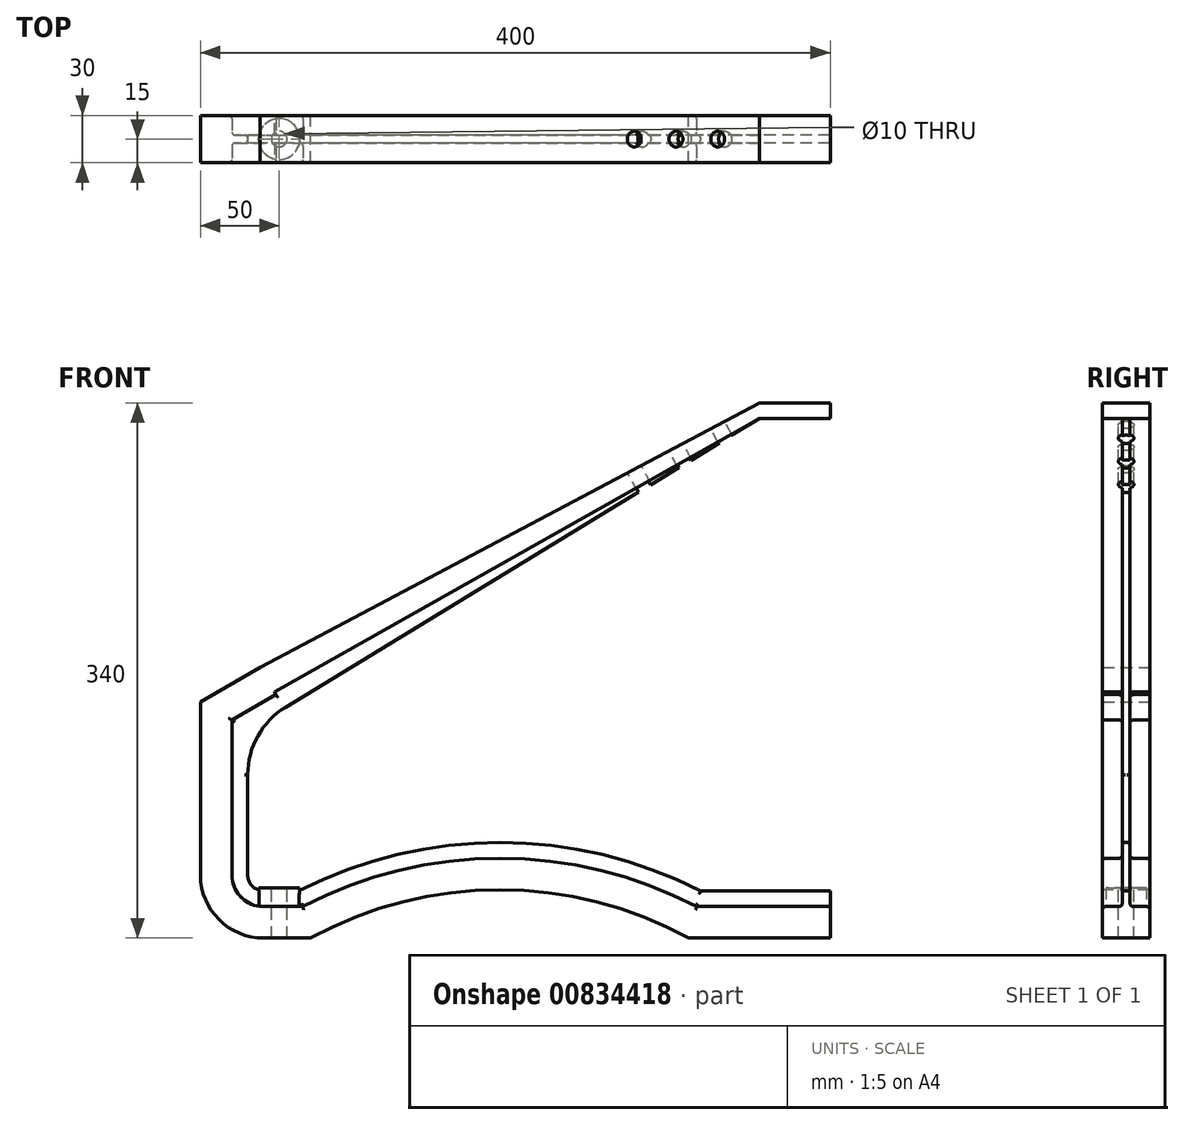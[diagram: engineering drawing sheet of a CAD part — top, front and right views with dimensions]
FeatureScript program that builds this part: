
annotation { "Feature Type Name" : "Feature", "Feature Type Description" : "" }
export const myFeature = defineFeature(function(context is Context, id is Id, definition is map)
    precondition{}
    {
        {
            var Q0;
            Q0=qCreatedBy(makeId("Right.planeOp"),FACE);
            var sketch = newSketch(context, id + "F0", { "sketchPlane" : qUnion([Q0])});
            skLineSegment(sketch, "E0", {"start": v(-15, 0) * mm, "end": v(15, 0) * mm});
            skLineSegment(sketch, "E1", {"start": v(15, 0) * mm, "end": v(15, 18) * mm});
            skLineSegment(sketch, "E2", {"start": v(13, 20) * mm, "end": v(4.5, 20) * mm});
            skLineSegment(sketch, "E3", {"start": v(2.5, 22) * mm, "end": v(2.5, 28) * mm});
            skLineSegment(sketch, "E4", {"start": v(0.5, 30) * mm, "end": v(-0.5, 30) * mm});
            skLineSegment(sketch, "E5", {"start": v(-2.5, 28) * mm, "end": v(-2.5, 22) * mm});
            skLineSegment(sketch, "E6", {"start": v(-4.5, 20) * mm, "end": v(-13, 20) * mm});
            skLineSegment(sketch, "E7", {"start": v(-15, 18) * mm, "end": v(-15, 0) * mm});
            skPoint(sketch, "E8.visualSharp", {"position": v(-15, 20) * mm});
            skArc(sketch, "E8.filletArc", {"start": v(-13, 20) * mm, "mid": v(-14.41, 19.41) * mm, "end": v(-15, 18) * mm});
            skPoint(sketch, "E9.visualSharp", {"position": v(15, 20) * mm});
            skArc(sketch, "E9.filletArc", {"start": v(15, 18) * mm, "mid": v(14.41, 19.41) * mm, "end": v(13, 20) * mm});
            skPoint(sketch, "E10.visualSharp", {"position": v(2.5, 20) * mm});
            skArc(sketch, "E10.filletArc", {"start": v(2.5, 22) * mm, "mid": v(3.09, 20.59) * mm, "end": v(4.5, 20) * mm});
            skPoint(sketch, "E11.visualSharp", {"position": v(-2.5, 20) * mm});
            skArc(sketch, "E11.filletArc", {"start": v(-4.5, 20) * mm, "mid": v(-3.09, 20.59) * mm, "end": v(-2.5, 22) * mm});
            skPoint(sketch, "E12.visualSharp", {"position": v(-2.5, 30) * mm});
            skArc(sketch, "E12.filletArc", {"start": v(-0.5, 30) * mm, "mid": v(-1.91, 29.41) * mm, "end": v(-2.5, 28) * mm});
            skPoint(sketch, "E13.visualSharp", {"position": v(2.5, 30) * mm});
            skArc(sketch, "E13.filletArc", {"start": v(2.5, 28) * mm, "mid": v(1.91, 29.41) * mm, "end": v(0.5, 30) * mm});
            skSolve(sketch);
        }
        {
            var Q0;
            Q0=qCreatedBy(makeId("Front.planeOp"),FACE);
            var sketch = newSketch(context, id + "F1", { "sketchPlane" : qUnion([Q0])});
            skLineSegment(sketch, "E14", {"start": v(0, 0) * mm, "end": v(-90, 0) * mm});
            skLineSegment(sketch, "E15", {"start": v(-400, 40) * mm, "end": v(-400, 150) * mm});
            skPoint(sketch, "E16.visualSharp", {"position": v(-400, 0) * mm});
            skArc(sketch, "E16.filletArc", {"start": v(-400, 40) * mm, "mid": v(-388.28, 11.72) * mm, "end": v(-360, 0) * mm});
            skArc(sketch, "E17", {"start": v(-90, 0) * mm, "mid": v(-210, 30.68) * mm, "end": v(-330, 0) * mm});
            skLineSegment(sketch, "E18.trimOffspring", {"start": v(-330, 0) * mm, "end": v(-360, 0) * mm});
            skLineSegment(sketch, "E19", {"start": v(-400, 150) * mm, "end": v(-362.06, 171.9) * mm});
            skSolve(sketch);
        }
        {
            var Q0;
            Q0=makeQuery(id+"F0.imprint","IMPRINT",FACE,{"disambiguationData":[TD([[makeQuery(id+"F0.imprint","IMPRINT",EDGE,{"derivedFrom":sQuery(id+"F0.wireOp",EDGE,"E0")}),1.0]])]});
            var Q1;
            Q1=sQuery(id+"F1.wireOp",EDGE,"E14");
            var Q2;
            Q2=sQuery(id+"F1.wireOp",EDGE,"E17");
            var Q3;
            Q3=sQuery(id+"F1.wireOp",EDGE,"E18.trimOffspring");
            var Q4;
            Q4=sQuery(id+"F1.wireOp",EDGE,"E16.filletArc");
            var Q5;
            Q5=sQuery(id+"F1.wireOp",EDGE,"E15");
            var Q6;
            Q6=sQuery(id+"F1.wireOp",EDGE,"E19");
            sweep(context, id + "F2", {"profiles" : qUnion([Q0]), "path" : qUnion([Q1, Q2, Q3, Q4, Q5, Q6])});
        }
        {
            var Q0;
            Q0=qCreatedBy(makeId("Front.planeOp"),FACE);
            var sketch = newSketch(context, id + "F3", { "sketchPlane" : qUnion([Q0])});
            skLineSegment(sketch, "E20", {"start": v(-362.06, 171.9) * mm, "end": v(-347.06, 145.92) * mm});
            skLineSegment(sketch, "E21", {"start": v(-347.06, 145.92) * mm, "end": v(-45, 330) * mm});
            skLineSegment(sketch, "E22", {"start": v(-45, 330) * mm, "end": v(0, 330) * mm});
            skLineSegment(sketch, "E23", {"start": v(-362.06, 171.9) * mm, "end": v(-45, 340) * mm});
            skLineSegment(sketch, "E24", {"start": v(-45, 340) * mm, "end": v(0, 340) * mm});
            skLineSegment(sketch, "E25", {"start": v(0, 340) * mm, "end": v(0, 330) * mm});
            skSolve(sketch);
        }
        {
            var Q0;
            Q0 = qSketchRegion(id + "F3", true);
            extrude(context, id + "F4", {"entities" : qUnion([Q0]), "operationType" : NewBodyOperationType.ADD, "endBound" : BoundingType.SYMMETRIC, "depth" : 30 * mm, "offsetDistance" : 25 * mm});
        }
        {
            var Q0;
            Q0=makeQuery(id+"F4.boolean.opBoolean","MERGE",FACE,{"derivedFrom":[makeQuery(id+"F2.opSweep","SWEPT_FACE",FACE,{"disambiguationData":[OSD([sQuery(id+"F0.wireOp",EDGE,"E7"),sQuery(id+"F1.wireOp",EDGE,"E14")])]}),makeQuery(id+"F4.opExtrude","CAP_FACE",FACE,{"disambiguationData":[OSD([sQuery(id+"F3.wireOp",EDGE,"R7F50b4I-J6sE-K8ba-BLaz-sTLGq43EXYzr"),sQuery(id+"F3.wireOp",EDGE,"5cav1WQY-YzdS-EUgr-7Edn-PjrxNAPj5FXO"),sQuery(id+"F3.wireOp",EDGE,"isAu9VLK-div0-A24P-HTb3-jHh66Twf6XfL"),sQuery(id+"F3.wireOp",EDGE,"TEhLIV82-5hpy-R3tn-7ywK-X99X9IhXxsMt"),sQuery(id+"F3.wireOp",EDGE,"mmeTSFns-Whpt-Msw0-SGPH-pD2UBuX707aM"),sQuery(id+"F3.wireOp",EDGE,"E20")])],"isStart":false})]});
            var sketch = newSketch(context, id + "F5", { "sketchPlane" : qUnion([Q0])});
            skLineSegment(sketch, "E26.0", {"start": v(-45, 330) * mm, "end": v(-353.06, 156.31) * mm});
            skLineSegment(sketch, "E27.0", {"start": v(-353.06, 156.31) * mm, "end": v(-347.06, 145.92) * mm});
            skLineSegment(sketch, "E28", {"start": v(-347.06, 145.92) * mm, "end": v(-45, 330) * mm});
            skSolve(sketch);
        }
        {
            var Q0;
            Q0=makeQuery(id+"F5.imprint","IMPRINT",FACE,{"disambiguationData":[TD([[makeQuery(id+"F5.imprint","IMPRINT",EDGE,{"derivedFrom":sQuery(id+"F5.wireOp",EDGE,"E26.0")}),1.0]])]});
            var Q1;
            Q1=makeQuery(id+"F2.opSweep","SWEPT_FACE",FACE,{"disambiguationData":[OSD([sQuery(id+"F0.wireOp",EDGE,"E5"),sQuery(id+"F1.wireOp",EDGE,"E14")])]});
            extrude(context, id + "F6", {"entities" : qUnion([Q0]), "operationType" : NewBodyOperationType.REMOVE, "oppositeDirection" : true, "depth" : 15 * mm, "endBoundEntityFace" : qUnion([Q1]), "offsetDistance" : 25 * mm});
        }
        {
            var Q0;
            Q0=makeQuery(id+"F4.boolean.opBoolean","MERGE",FACE,{"derivedFrom":[makeQuery(id+"F2.opSweep","SWEPT_FACE",FACE,{"disambiguationData":[OSD([sQuery(id+"F0.wireOp",EDGE,"E1"),sQuery(id+"F1.wireOp",EDGE,"E14")])]}),makeQuery(id+"F4.opExtrude","CAP_FACE",FACE,{"disambiguationData":[OSD([sQuery(id+"F3.wireOp",EDGE,"R7F50b4I-J6sE-K8ba-BLaz-sTLGq43EXYzr"),sQuery(id+"F3.wireOp",EDGE,"5cav1WQY-YzdS-EUgr-7Edn-PjrxNAPj5FXO"),sQuery(id+"F3.wireOp",EDGE,"isAu9VLK-div0-A24P-HTb3-jHh66Twf6XfL"),sQuery(id+"F3.wireOp",EDGE,"TEhLIV82-5hpy-R3tn-7ywK-X99X9IhXxsMt"),sQuery(id+"F3.wireOp",EDGE,"mmeTSFns-Whpt-Msw0-SGPH-pD2UBuX707aM"),sQuery(id+"F3.wireOp",EDGE,"E20")])],"isStart":true})]});
            var sketch = newSketch(context, id + "F7", { "sketchPlane" : qUnion([Q0])});
            skLineSegment(sketch, "E29.0", {"start": v(353.06, 156.31) * mm, "end": v(347.06, 145.92) * mm});
            skLineSegment(sketch, "E30.0", {"start": v(45, 330) * mm, "end": v(347.06, 145.92) * mm});
            skLineSegment(sketch, "E31", {"start": v(45, 330) * mm, "end": v(353.06, 156.31) * mm});
            skSolve(sketch);
        }
        {
            var Q0;
            Q0 = qSketchRegion(id + "F7", true);
            var Q1;
            Q1=makeQuery(id+"F2.opSweep","SWEPT_FACE",FACE,{"disambiguationData":[OSD([sQuery(id+"F0.wireOp",EDGE,"E3"),sQuery(id+"F1.wireOp",EDGE,"E14")])]});
            extrude(context, id + "F8", {"entities" : qUnion([Q0]), "operationType" : NewBodyOperationType.REMOVE, "endBound" : BoundingType.UP_TO_SURFACE, "oppositeDirection" : true, "depth" : 25 * mm, "endBoundEntityFace" : qUnion([Q1]), "offsetDistance" : 25 * mm});
        }
        {
            var Q0;
            Q0=qCreatedBy(makeId("Front.planeOp"),FACE);
            var sketch = newSketch(context, id + "F9", { "sketchPlane" : qUnion([Q0])});
            skPoint(sketch, "E32.orphan", {"position": v(-370, 40) * mm});
            skLineSegment(sketch, "E33.0", {"start": v(-372, 133.83) * mm, "end": v(-348.06, 147.65) * mm});
            skLineSegment(sketch, "E34.0", {"start": v(-347.06, 145.92) * mm, "end": v(-348.06, 147.65) * mm});
            skLineSegment(sketch, "E35.0", {"start": v(-370, 132.68) * mm, "end": v(-347.06, 145.92) * mm});
            skLineSegment(sketch, "E36.0", {"start": v(-370, 132.68) * mm, "end": v(-372, 133.83) * mm});
            skSolve(sketch);
        }
        {
            var Q0;
            Q0 = qSketchRegion(id + "F9", true);
            var Q1;
            {var subQ0=sQuery(id+"F1.wireOp",EDGE,"E14");var subQ1=sQuery(id+"F0.wireOp",EDGE,"E5");Q1=makeQuery(id+"F6.boolean.opBoolean","MERGE",FACE,{"derivedFrom":[makeQuery(id+"F2.opSweep","SWEPT_FACE",FACE,{"disambiguationData":[OSD([subQ1,subQ0])]}),makeQuery(id+"F6.opExtrude","CAP_FACE",FACE,{"disambiguationData":[OSD([subQ1,subQ0])],"isStart":false})]});}
            extrude(context, id + "F10", {"entities" : qUnion([Q0]), "operationType" : NewBodyOperationType.ADD, "endBound" : BoundingType.UP_TO_SURFACE, "depth" : 25 * mm, "endBoundEntityFace" : qUnion([Q1]), "offsetDistance" : 25 * mm});
        }
        {
            var Q0;
            Q0=makeQuery(id+"F2.opSweep","SWEPT_BODY",BODY,{"disambiguationData":[OSD([sQuery(id+"F0.wireOp",EDGE,"E0"),sQuery(id+"F0.wireOp",EDGE,"E1"),sQuery(id+"F0.wireOp",EDGE,"E2"),sQuery(id+"F0.wireOp",EDGE,"E3"),sQuery(id+"F0.wireOp",EDGE,"E4"),sQuery(id+"F0.wireOp",EDGE,"E5"),sQuery(id+"F0.wireOp",EDGE,"E6"),sQuery(id+"F0.wireOp",EDGE,"E7"),sQuery(id+"F0.wireOp",EDGE,"E8.filletArc"),sQuery(id+"F0.wireOp",EDGE,"E9.filletArc"),sQuery(id+"F0.wireOp",EDGE,"E10.filletArc"),sQuery(id+"F0.wireOp",EDGE,"E11.filletArc"),sQuery(id+"F0.wireOp",EDGE,"E12.filletArc"),sQuery(id+"F0.wireOp",EDGE,"E13.filletArc"),sQuery(id+"F1.wireOp",EDGE,"E19")])]});
            var Q1;
            Q1=qCreatedBy(makeId("Front.planeOp"),FACE);
            mirror(context, id + "F11", {"operationType" : NewBodyOperationType.ADD, "entities" : qUnion([Q0]), "mirrorPlane" : qUnion([Q1])});
        }
        {
            var Q0;
            {var subQ0=sQuery(id+"F1.wireOp",EDGE,"E14");var subQ1=sQuery(id+"F0.wireOp",EDGE,"E5");Q0=makeQuery(id+"F10.boolean.opBoolean","MERGE",FACE,{"derivedFrom":[makeQuery(id+"F6.boolean.opBoolean","MERGE",FACE,{"derivedFrom":[makeQuery(id+"F2.opSweep","SWEPT_FACE",FACE,{"disambiguationData":[OSD([subQ1,subQ0])]}),makeQuery(id+"F6.opExtrude","CAP_FACE",FACE,{"disambiguationData":[OSD([subQ1,subQ0])],"isStart":false})]}),makeQuery(id+"F10.opExtrude","CAP_FACE",FACE,{"disambiguationData":[OSD([subQ1,subQ0])],"isStart":false})]});}
            var sketch = newSketch(context, id + "F12", { "sketchPlane" : qUnion([Q0])});
            skPoint(sketch, "E37.orphan", {"position": v(-372, 40) * mm});
            skLineSegment(sketch, "E38.0", {"start": v(-370, 132.68) * mm, "end": v(-372, 133.83) * mm});
            skLineSegment(sketch, "E39.0", {"start": v(-372, 103.48) * mm, "end": v(-372, 133.83) * mm});
            skLineSegment(sketch, "E40.0.0", {"start": v(-370, 103.48) * mm, "end": v(-370, 132.68) * mm});
            skLineSegment(sketch, "E40.0.2", {"start": v(-372, 133.83) * mm, "end": v(-372, 103.48) * mm});
            skLineSegment(sketch, "E40.0.3", {"start": v(-372, 40) * mm, "end": v(-370, 40) * mm});
            skLineSegment(sketch, "E41", {"start": v(-372, 103.48) * mm, "end": v(-370, 103.48) * mm});
            skSolve(sketch);
        }
        {
            var Q0;
            Q0 = qSketchRegion(id + "F12", true);
            var Q1;
            {var subQ0=sQuery(id+"F1.wireOp",EDGE,"E14");var subQ1=sQuery(id+"F0.wireOp",EDGE,"E5");var subQ2=sQuery(id+"F0.wireOp",EDGE,"E3");Q1=makeQuery(id+"F11.boolean.opBoolean","MERGE",FACE,{"derivedFrom":[makeQuery(id+"F8.boolean.opBoolean","MERGE",FACE,{"derivedFrom":[makeQuery(id+"F2.opSweep","SWEPT_FACE",FACE,{"disambiguationData":[OSD([subQ2,subQ0])]}),makeQuery(id+"F8.opExtrude","CAP_FACE",FACE,{"disambiguationData":[OSD([subQ2,subQ0])],"isStart":false})]}),makeQuery(id+"F11.opPattern","COPY",FACE,{"derivedFrom":makeQuery(id+"F10.boolean.opBoolean","MERGE",FACE,{"derivedFrom":[makeQuery(id+"F6.boolean.opBoolean","MERGE",FACE,{"derivedFrom":[makeQuery(id+"F2.opSweep","SWEPT_FACE",FACE,{"disambiguationData":[OSD([subQ1,subQ0])]}),makeQuery(id+"F6.opExtrude","CAP_FACE",FACE,{"disambiguationData":[OSD([subQ1,subQ0])],"isStart":false})]}),makeQuery(id+"F10.opExtrude","CAP_FACE",FACE,{"disambiguationData":[OSD([subQ1,subQ0])],"isStart":false})]}),"instanceName":"1"})]});}
            extrude(context, id + "F13", {"entities" : qUnion([Q0]), "operationType" : NewBodyOperationType.ADD, "endBound" : BoundingType.UP_TO_SURFACE, "oppositeDirection" : true, "depth" : 2.7 * mm, "endBoundEntityFace" : qUnion([Q1]), "offsetDistance" : 25 * mm});
        }
        {
            var Q0;
            {var subQ0=sQuery(id+"F9.wireOp",EDGE,"E35.0");var subQ1=makeQuery(id+"F10.opExtrude","SWEPT_EDGE",EDGE,{"disambiguationData":[OSD([subQ0,sQuery(id+"F9.wireOp",EDGE,"E36.0")])]});Q0=makeQuery(id+"F13.boolean.opBoolean","MERGE",EDGE,{"derivedFrom":[makeQuery(id+"F2.opSweep","MID_CAP_EDGE",EDGE,{"disambiguationData":[OSD([sQuery(id+"F0.wireOp",EDGE,"E4"),sQuery(id+"F1.wireOp",VERTEX,"E19.start")])],"capPos":5.0}),subQ1,makeQuery(id+"F11.opPattern","COPY",EDGE,{"derivedFrom":subQ1,"instanceName":"1"}),makeQuery(id+"F13.opExtrude","SWEPT_EDGE",EDGE,{"disambiguationData":[OSD([sQuery(id+"F0.wireOp",EDGE,"E5"),sQuery(id+"F1.wireOp",EDGE,"E14"),subQ0,sQuery(id+"F12.wireOp",EDGE,"E40.0.0"),sQuery(id+"F12.wireOp",EDGE,"E38.0")])]})]});}
            fillet(context, id + "F14", {"entities" : qUnion([Q0]), "radius" : 50 * mm, "tangentPropagation" : true, "allowEdgeOverflow" : false});
        }
        {
            var Q0;
            Q0=makeQuery(id+"F2.opSweep","SWEPT_FACE",FACE,{"disambiguationData":[OSD([sQuery(id+"F0.wireOp",EDGE,"E6"),sQuery(id+"F1.wireOp",EDGE,"E18.trimOffspring")])]});
            var sketch = newSketch(context, id + "F15", { "sketchPlane" : qUnion([Q0])});
            skCircle(sketch, "E42", {"center": v(-350, 0) * mm, "radius": 13 * mm});
            skSolve(sketch);
        }
        {
            var Q0;
            Q0 = qSketchRegion(id + "F15", true);
            var Q1;
            Q1=makeQuery(id+"F2.opSweep","SWEPT_FACE",FACE,{"disambiguationData":[OSD([sQuery(id+"F0.wireOp",EDGE,"E4"),sQuery(id+"F1.wireOp",EDGE,"E18.trimOffspring")])]});
            extrude(context, id + "F16", {"entities" : qUnion([Q0]), "operationType" : NewBodyOperationType.ADD, "depth" : 12 * mm, "endBoundEntityFace" : qUnion([Q1]), "offsetDistance" : 25 * mm});
        }
        {
            var Q0;
            Q0=makeQuery(id+"F16.opExtrude","CAP_FACE",FACE,{"disambiguationData":[OSD([sQuery(id+"F15.wireOp",EDGE,"E42")])],"isStart":false});
            var sketch = newSketch(context, id + "F17", { "sketchPlane" : qUnion([Q0])});
            skCircle(sketch, "E43", {"center": v(-350, 0) * mm, "radius": 5 * mm});
            skSolve(sketch);
        }
        {
            var Q0;
            Q0 = qSketchRegion(id + "F17", true);
            extrude(context, id + "F18", {"entities" : qUnion([Q0]), "operationType" : NewBodyOperationType.REMOVE, "endBound" : BoundingType.UP_TO_NEXT, "oppositeDirection" : true, "depth" : 25 * mm, "offsetDistance" : 25 * mm});
        }
        {
            var Q0;
            Q0=makeQuery(id+"F4.opExtrude","SWEPT_FACE",FACE,{"disambiguationData":[OSD([sQuery(id+"F3.wireOp",EDGE,"E23")])]});
            var sketch = newSketch(context, id + "F19", { "sketchPlane" : qUnion([Q0])});
            skCircle(sketch, "E44", {"center": v(89.5, 0) * mm, "radius": 5 * mm});
            skCircle(sketch, "E45", {"center": v(59.5, 0) * mm, "radius": 5 * mm});
            skCircle(sketch, "E46", {"center": v(29.5, 0) * mm, "radius": 5 * mm});
            skSolve(sketch);
        }
        {
            var Q0;
            Q0 = qSketchRegion(id + "F19", true);
            extrude(context, id + "F20", {"entities" : qUnion([Q0]), "operationType" : NewBodyOperationType.REMOVE, "oppositeDirection" : true, "depth" : 25 * mm, "offsetDistance" : 25 * mm});
        }
    });
